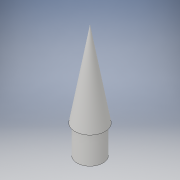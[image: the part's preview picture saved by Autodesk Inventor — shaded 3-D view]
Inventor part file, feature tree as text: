
AUTODESK INVENTOR PART (.ipt)
format: ipt  version: 2017 (Build 210142000, 142)  size: 138,752 bytes
history: native  units: in
note: dims shown in document units (in); Inventor stores cm internally (conversion verified against a paired STEP export)
features: sketch x2, revolve x1, extrude x1
ambient origin geometry x8: Origin, YZ Plane, XZ Plane, XY Plane, X Axis, Y Axis, Z Axis, Center Point
bodies: Solid1 (feature_tree)
feature tree (4):
  revolve  "Revolution1"  Angle=90.0deg
  extrude  "Extrusion1"  TaperAngle=0.0deg  [1 undecoded]
  sketch  "Sketch1"  dims[d0=3.0in d1=90.0deg]
  sketch  "Sketch2"  dims[d2=0.53in d3=0.0in d4=0.457in d5=1.0in d6=0.05in d7=0.05in d8=90.0deg d21=0.05in d22=0.0in]
note: 1 required parameter value undecoded (feature->parameter linkage not recoverable at this tier; creation-order binding heuristic only, values carry confidence <= 0.55)
